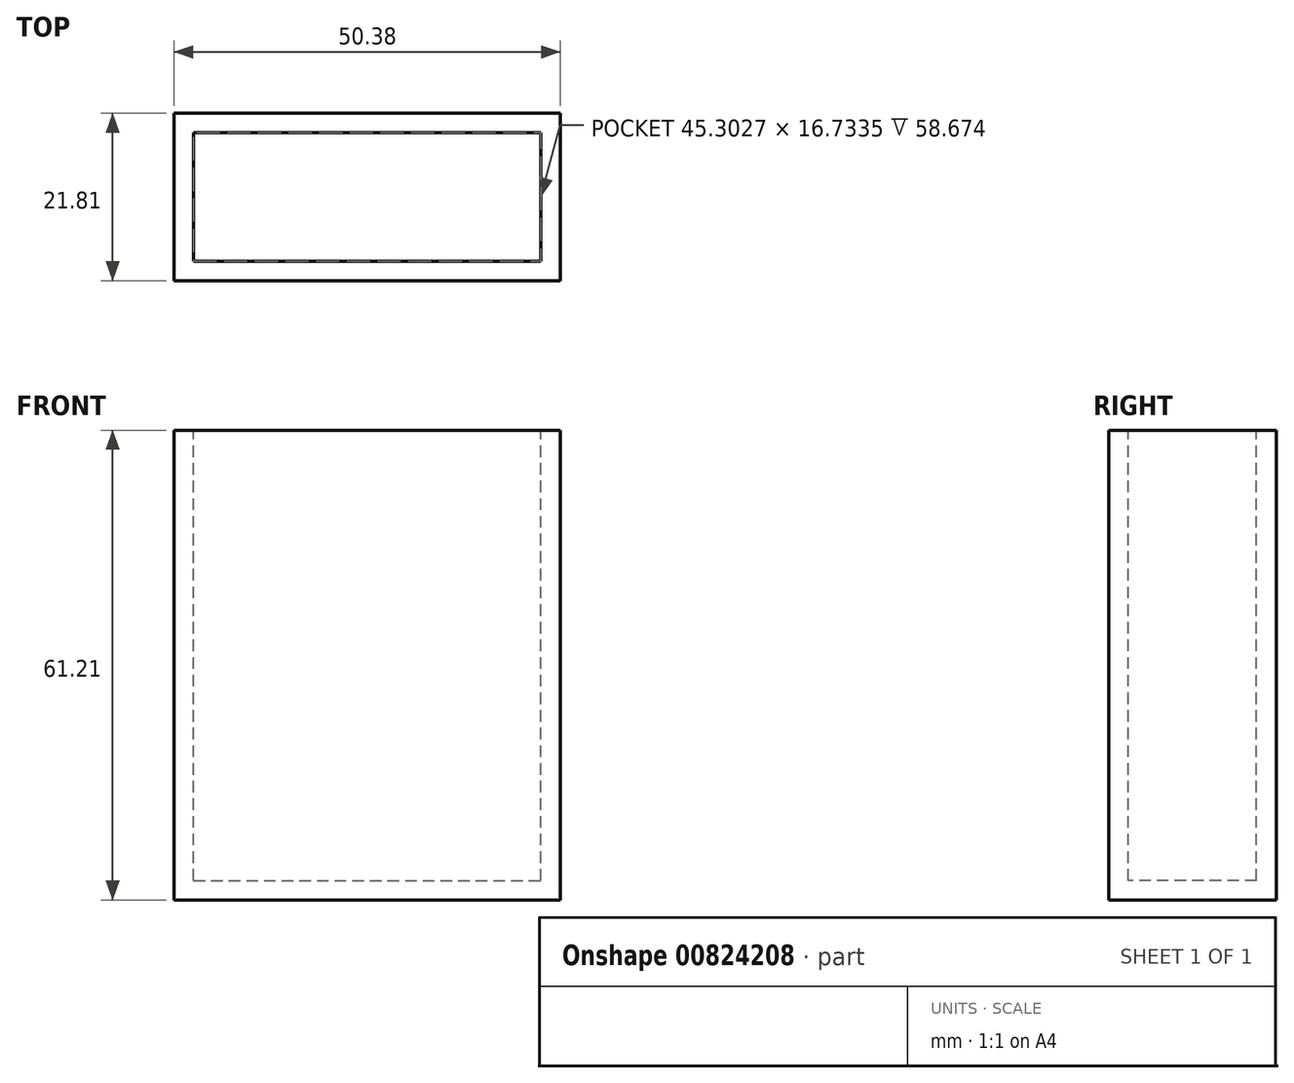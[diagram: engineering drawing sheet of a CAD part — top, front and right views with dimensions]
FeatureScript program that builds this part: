
annotation { "Feature Type Name" : "Feature", "Feature Type Description" : "" }
export const myFeature = defineFeature(function(context is Context, id is Id, definition is map)
    precondition{}
    {
        {
            var Q0;
            Q0=qCreatedBy(makeId("Top.planeOp"),FACE);
            var sketch = newSketch(context, id + "F0", { "sketchPlane" : qUnion([Q0])});
            skLineSegment(sketch, "E0.bottom", {"start": v(0, 0) * mm, "end": v(50.38, 0) * mm});
            skLineSegment(sketch, "E0.top", {"start": v(0, -21.81) * mm, "end": v(50.38, -21.81) * mm});
            skLineSegment(sketch, "E0.left", {"start": v(0, 0) * mm, "end": v(0, -21.81) * mm});
            skLineSegment(sketch, "E0.right", {"start": v(50.38, 0) * mm, "end": v(50.38, -21.81) * mm});
            skSolve(sketch);
        }
        {
            var Q0;
            Q0=makeQuery(id+"F0.imprint","IMPRINT",FACE,{"disambiguationData":[TD([[makeQuery(id+"F0.imprint","IMPRINT",EDGE,{"derivedFrom":sQuery(id+"F0.wireOp",EDGE,"E0.bottom")}),-1.0]])]});
            extrude(context, id + "F1", {"entities" : qUnion([Q0]), "oppositeDirection" : true, "depth" : 61.2 * mm, "offsetDistance" : 25.4 * mm});
        }
        {
            var Q0;
            Q0=makeQuery(id+"F1.opExtrude","CAP_FACE",FACE,{"disambiguationData":[OSD([sQuery(id+"F0.wireOp",EDGE,"E0.bottom"),sQuery(id+"F0.wireOp",EDGE,"E0.top"),sQuery(id+"F0.wireOp",EDGE,"E0.left"),sQuery(id+"F0.wireOp",EDGE,"E0.right")])],"isStart":true});
            shell(context, id + "F2", {"entities" : qUnion([Q0]), "thickness" : 2.54 * mm});
        }
    });
